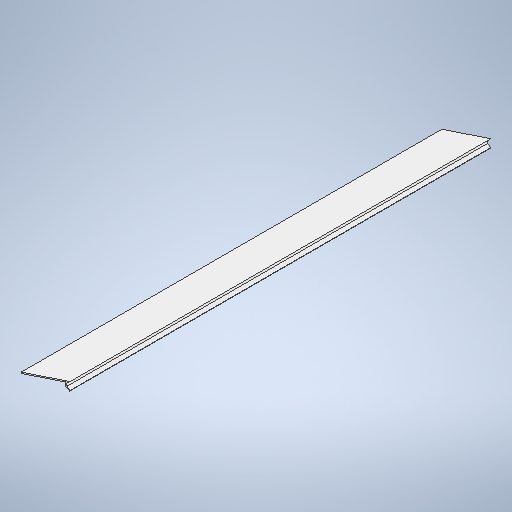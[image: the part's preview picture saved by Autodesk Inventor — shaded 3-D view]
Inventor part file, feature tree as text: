
AUTODESK INVENTOR PART (.ipt)
format: ipt  version: 2025 (Build 290162010, 162A)  size: 286,720 bytes
history: native  units: in
note: dims shown in document units (in); Inventor stores cm internally (conversion verified against a paired STEP export)
features: extrude x1, sketch x1
ambient origin geometry x8: Origin, YZ Plane, XZ Plane, XY Plane, X Axis, Y Axis, Z Axis, Center Point
bodies: Body1 (feature_tree)
feature tree (2):
  extrude  "Extrusion2"  Depth=0.125in
  sketch  "Sketch1"  dims[d5=5.5in d17=3.5in d19=132.0in d23=1.194in d28=1.8188in d33=42.875in d36=1.0in d37=0.625in d49=0.125in d50=0.125in d51=0.125in d52=0.125in d54=0.333in d55=0.333in d59=48.919in d60=0.0in d61=0.333in d62=6.0in d63=0.125in d65=0.5in d73=6.0in d74=0.5in d75=0.125in d76=0.125in d78=0.333in d79=0.333in d80=0.333in]
